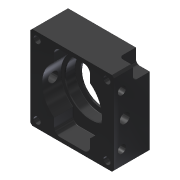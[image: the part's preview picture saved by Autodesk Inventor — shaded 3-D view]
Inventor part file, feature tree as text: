
AUTODESK INVENTOR PART (.ipt)
format: ipt  version: 2013 (Build 170138000, 138)  size: 270,848 bytes
history: native  units: in
note: dims shown in document units (in); Inventor stores cm internally (conversion verified against a paired STEP export)
features: hole x1, other x1, imported_body x1
ambient origin geometry x8: Origin, YZ Plane, XZ Plane, XY Plane, X Axis, Y Axis, Z Axis, Center Point
feature tree (3):
  hole  "Hole1"  [1 undecoded]
  other  "217-2625-001 Rev11"
  imported_body  "Base1"
note: 1 required parameter value undecoded (feature->parameter linkage not recoverable at this tier; creation-order binding heuristic only, values carry confidence <= 0.55)
